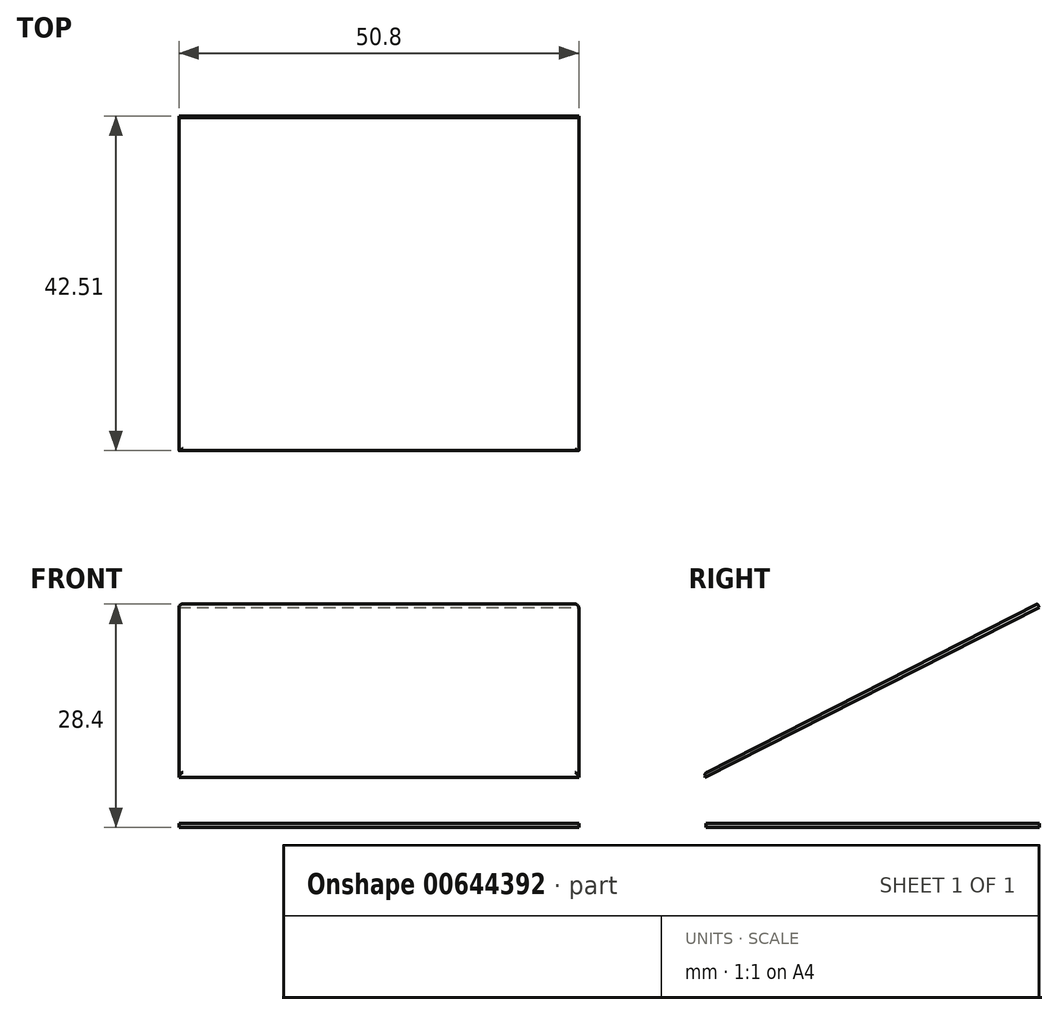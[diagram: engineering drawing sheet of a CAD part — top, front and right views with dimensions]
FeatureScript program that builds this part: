
annotation { "Feature Type Name" : "Feature", "Feature Type Description" : "" }
export const myFeature = defineFeature(function(context is Context, id is Id, definition is map)
    precondition{}
    {
        {
            var Q0;
            Q0=qCreatedBy(makeId("Right.planeOp"),FACE);
            var sketch = newSketch(context, id + "F0", { "sketchPlane" : qUnion([Q0])});
            skLineSegment(sketch, "E0", {"start": v(-42.38, 0) * mm, "end": v(0, 0) * mm});
            skLineSegment(sketch, "E1", {"start": v(-42.46, 5.85) * mm, "end": v(0, 27.44) * mm});
            skArc(sketch, "E2", {"start": v(0, 0) * mm, "mid": v(4.63, 13.72) * mm, "end": v(0, 27.44) * mm});
            skSolve(sketch);
        }
        {
            var Q0;
            Q0=sQuery(id+"F0.wireOp",EDGE,"E1");
            var Q1;
            Q1=sQuery(id+"F0.wireOp",EDGE,"E0");
            var Q2;
            Q2=sQuery(id+"F0.wireOp",EDGE,"E2");
            extrude(context, id + "F1", {"bodyType" : ToolBodyType.SURFACE, "surfaceEntities" : qUnion([Q0, Q1, Q2]), "depth" : 50.8 * mm, "offsetDistance" : 25.4 * mm});
        }
        {
            var Q0;
            Q0=makeQuery(id+"F1.opExtrude","SWEPT_FACE",FACE,{"disambiguationData":[OSD([sQuery(id+"F0.wireOp",EDGE,"E1")])]});
            extrude(context, id + "F2", {"entities" : qUnion([Q0]), "depth" : 0.5 * mm, "offsetDistance" : 25.4 * mm});
        }
        {
            var Q0;
            Q0=makeQuery(id+"F1.opExtrude","SWEPT_FACE",FACE,{"disambiguationData":[OSD([sQuery(id+"F0.wireOp",EDGE,"E0")])]});
            extrude(context, id + "F3", {"entities" : qUnion([Q0]), "depth" : 0.5 * mm, "offsetDistance" : 25.4 * mm});
        }
        {
            var Q0;
            {var subQ0=sQuery(id+"F0.wireOp",EDGE,"E1");Q0=makeQuery(id+"F2.opExtrude","CAP_EDGE",EDGE,{"disambiguationData":[OSD([subQ0]),TDD([makeQuery(id+"F1.opExtrude","CAP_EDGE",EDGE,{"disambiguationData":[OSD([subQ0])],"isStart":false})])],"isStart":false});}
            var Q1;
            Q1=makeQuery(id+"F2.opExtrude","CAP_EDGE",EDGE,{"disambiguationData":[OSD([sQuery(id+"F0.wireOp",VERTEX,"E1.start")])],"isStart":false});
            var Q2;
            {var subQ0=sQuery(id+"F0.wireOp",EDGE,"E1");Q2=makeQuery(id+"F2.opExtrude","CAP_EDGE",EDGE,{"disambiguationData":[OSD([subQ0]),TDD([makeQuery(id+"F1.opExtrude","CAP_EDGE",EDGE,{"disambiguationData":[OSD([subQ0])],"isStart":true})])],"isStart":false});}
            var Q3;
            {var subQ0=sQuery(id+"F0.wireOp",EDGE,"E0");Q3=makeQuery(id+"F3.opExtrude","SWEPT_FACE",FACE,{"disambiguationData":[OSD([subQ0]),TDD([makeQuery(id+"F1.opExtrude","CAP_EDGE",EDGE,{"disambiguationData":[OSD([subQ0])],"isStart":false})])]});}
            var Q4;
            Q4=makeQuery(id+"F3.opExtrude","CAP_EDGE",EDGE,{"disambiguationData":[OSD([sQuery(id+"F0.wireOp",VERTEX,"E0.start")])],"isStart":false});
            var Q5;
            {var subQ0=sQuery(id+"F0.wireOp",EDGE,"E0");Q5=makeQuery(id+"F3.opExtrude","CAP_EDGE",EDGE,{"disambiguationData":[OSD([subQ0]),TDD([makeQuery(id+"F1.opExtrude","CAP_EDGE",EDGE,{"disambiguationData":[OSD([subQ0])],"isStart":true})])],"isStart":false});}
            fillet(context, id + "F4", {"entities" : qUnion([Q0, Q1, Q2, Q3, Q4, Q5]), "radius" : 0.5 * mm, "tangentPropagation" : true, "allowEdgeOverflow" : false});
        }
    });
